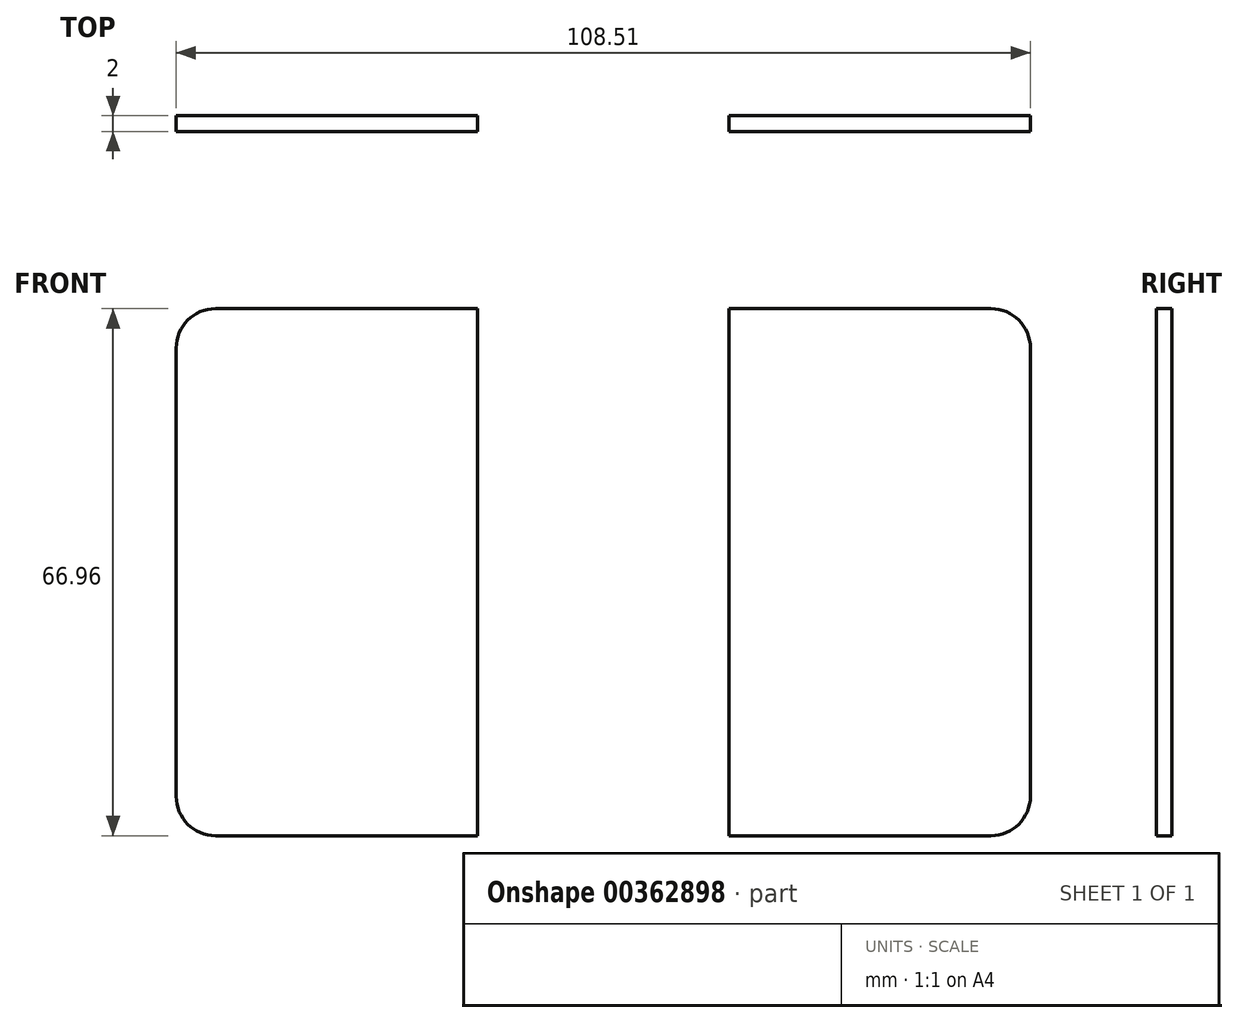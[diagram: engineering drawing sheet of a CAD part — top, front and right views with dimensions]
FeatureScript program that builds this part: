
annotation { "Feature Type Name" : "Feature", "Feature Type Description" : "" }
export const myFeature = defineFeature(function(context is Context, id is Id, definition is map)
    precondition{}
    {
        {
            var Q0;
            Q0=qCreatedBy(makeId("Front.planeOp"),FACE);
            var sketch = newSketch(context, id + "F0", { "sketchPlane" : qUnion([Q0])});
            skLineSegment(sketch, "E0.bottom", {"start": v(-33.29, 59.88) * mm, "end": v(0, 59.88) * mm});
            skLineSegment(sketch, "E0.top", {"start": v(-33.29, -7.08) * mm, "end": v(0, -7.08) * mm});
            skLineSegment(sketch, "E0.left", {"start": v(-38.29, 54.88) * mm, "end": v(-38.29, -2.08) * mm});
            skLineSegment(sketch, "E0.right", {"start": v(0, 59.88) * mm, "end": v(0, -7.08) * mm});
            skLineSegment(sketch, "E1.bottom", {"start": v(0, -7.08) * mm, "end": v(-3.63, -7.08) * mm});
            skLineSegment(sketch, "E1.top", {"start": v(0, -18.5) * mm, "end": v(-3.63, -18.5) * mm});
            skLineSegment(sketch, "E1.left", {"start": v(0, -7.08) * mm, "end": v(0, -18.5) * mm});
            skLineSegment(sketch, "E1.right", {"start": v(-3.63, -7.08) * mm, "end": v(-3.63, -18.5) * mm});
            skLineSegment(sketch, "E2", {"start": v(15.97, 74.94) * mm, "end": v(15.97, -60.06) * mm});
            skLineSegment(sketch, "E3.MirrorCS", {"start": v(65.22, 59.88) * mm, "end": v(31.94, 59.88) * mm});
            skLineSegment(sketch, "E4.MirrorCS", {"start": v(31.94, 59.88) * mm, "end": v(31.94, -7.08) * mm});
            skLineSegment(sketch, "E5.MirrorCS", {"start": v(70.22, 54.88) * mm, "end": v(70.22, -2.08) * mm});
            skLineSegment(sketch, "E6.MirrorCS", {"start": v(65.22, -7.08) * mm, "end": v(31.94, -7.08) * mm});
            skLineSegment(sketch, "E7.MirrorCS", {"start": v(31.94, -7.08) * mm, "end": v(35.56, -7.08) * mm});
            skLineSegment(sketch, "E8.MirrorCS", {"start": v(35.56, -7.08) * mm, "end": v(35.56, -18.5) * mm});
            skLineSegment(sketch, "E9.MirrorCS", {"start": v(31.94, -7.08) * mm, "end": v(31.94, -18.5) * mm});
            skLineSegment(sketch, "E10.MirrorCS", {"start": v(31.94, -18.5) * mm, "end": v(35.56, -18.5) * mm});
            skPoint(sketch, "E11.visualSharp", {"position": v(-38.29, 59.88) * mm});
            skArc(sketch, "E11.filletArc", {"start": v(-33.29, 59.88) * mm, "mid": v(-36.82, 58.41) * mm, "end": v(-38.29, 54.88) * mm});
            skPoint(sketch, "E12.visualSharp", {"position": v(70.22, 59.88) * mm});
            skArc(sketch, "E12.filletArc", {"start": v(70.22, 54.88) * mm, "mid": v(68.76, 58.41) * mm, "end": v(65.22, 59.88) * mm});
            skPoint(sketch, "E13.visualSharp", {"position": v(70.22, -7.08) * mm});
            skArc(sketch, "E13.filletArc", {"start": v(65.22, -7.08) * mm, "mid": v(68.76, -5.61) * mm, "end": v(70.22, -2.08) * mm});
            skPoint(sketch, "E14.visualSharp", {"position": v(-38.29, -7.08) * mm});
            skArc(sketch, "E14.filletArc", {"start": v(-38.29, -2.08) * mm, "mid": v(-36.82, -5.61) * mm, "end": v(-33.29, -7.08) * mm});
            skSolve(sketch);
        }
        {
            var Q0;
            Q0=makeQuery(id+"F0.imprint","IMPRINT",FACE,{"disambiguationData":[TD([[makeQuery(id+"F0.imprint","IMPRINT",EDGE,{"derivedFrom":sQuery(id+"F0.wireOp",EDGE,"E0.bottom")}),-1.0]])]});
            var Q1;
            Q1=makeQuery(id+"F0.imprint","IMPRINT",FACE,{"disambiguationData":[TD([[makeQuery(id+"F0.imprint","IMPRINT",EDGE,{"derivedFrom":sQuery(id+"F0.wireOp",EDGE,"E1.bottom")}),1.0]])]});
            var Q2;
            Q2=makeQuery(id+"F0.imprint","IMPRINT",FACE,{"disambiguationData":[TD([[makeQuery(id+"F0.imprint","IMPRINT",EDGE,{"derivedFrom":sQuery(id+"F0.wireOp",EDGE,"E3.MirrorCS")}),1.0]])]});
            var Q3;
            Q3=makeQuery(id+"F0.imprint","IMPRINT",FACE,{"disambiguationData":[TD([[makeQuery(id+"F0.imprint","IMPRINT",EDGE,{"derivedFrom":sQuery(id+"F0.wireOp",EDGE,"E7.MirrorCS")}),-1.0]])]});
            extrude(context, id + "F1", {"entities" : qUnion([Q0, Q1, Q2, Q3]), "depth" : 2 * mm});
        }
    });
